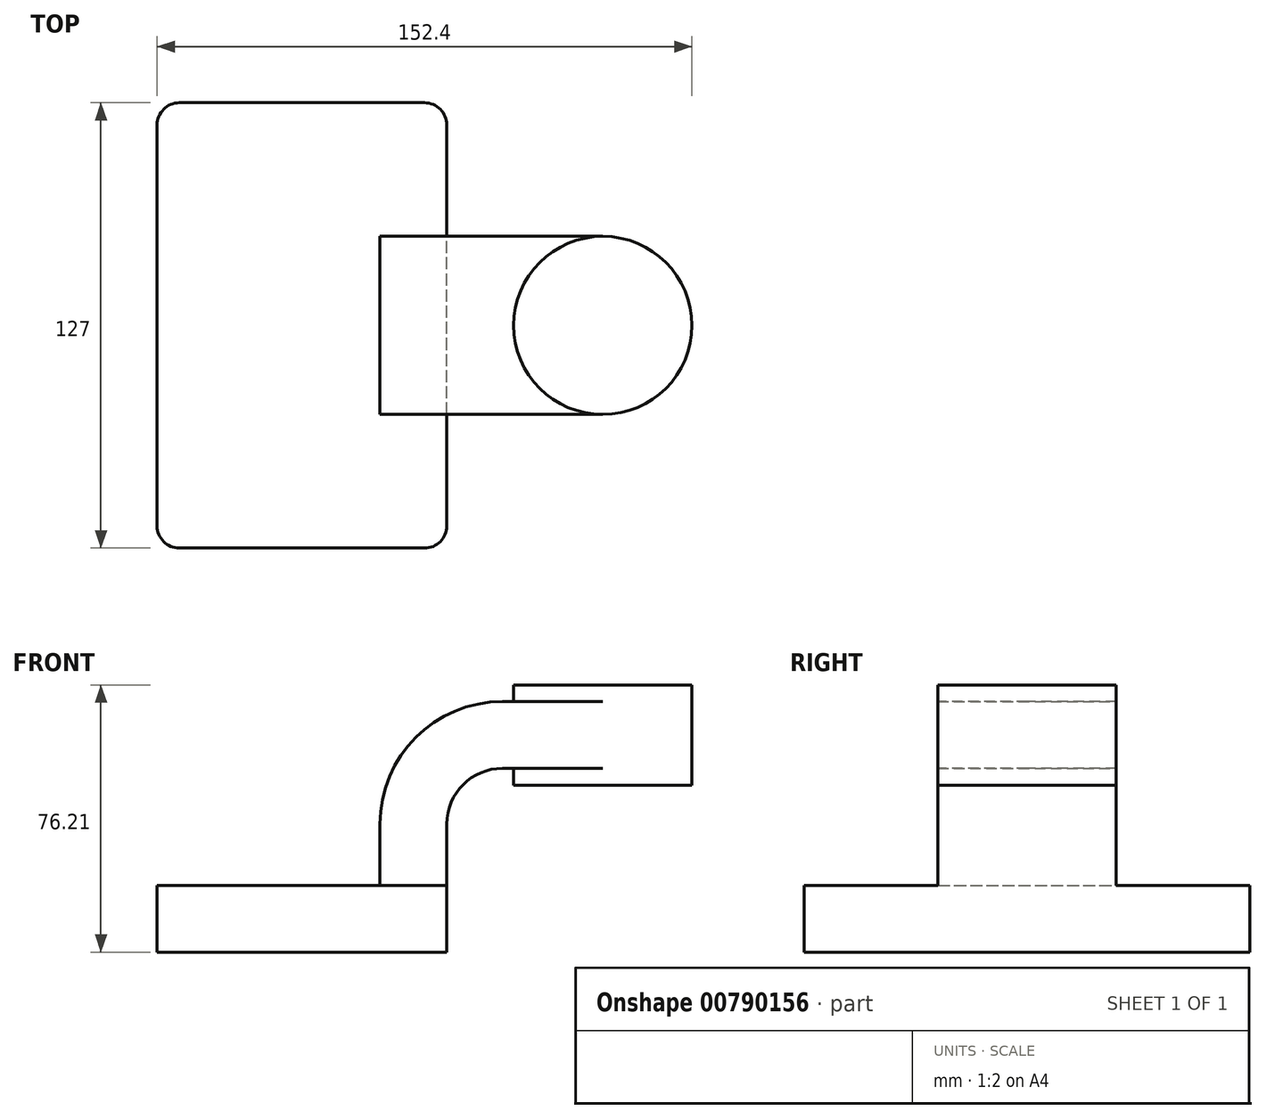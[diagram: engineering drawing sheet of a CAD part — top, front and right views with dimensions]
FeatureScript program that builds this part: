
annotation { "Feature Type Name" : "Feature", "Feature Type Description" : "" }
export const myFeature = defineFeature(function(context is Context, id is Id, definition is map)
    precondition{}
    {
        {
            var Q0;
            Q0=qCreatedBy(makeId("Front.planeOp"),FACE);
            var sketch = newSketch(context, id + "F0", { "sketchPlane" : qUnion([Q0])});
            skLineSegment(sketch, "E0.bottom", {"start": v(-41.27, -9.53) * mm, "end": v(41.28, -9.53) * mm});
            skLineSegment(sketch, "E0.top", {"start": v(-41.28, 9.52) * mm, "end": v(41.28, 9.52) * mm});
            skLineSegment(sketch, "E0.left", {"start": v(-41.28, -9.53) * mm, "end": v(-41.28, 9.52) * mm});
            skLineSegment(sketch, "E0.right", {"start": v(41.28, -9.53) * mm, "end": v(41.28, 9.52) * mm});
            skPoint(sketch, "E0.middle", {"position": v(0, 0) * mm});
            skLineSegment(sketch, "E1.bottom", {"start": v(60.32, 38.1) * mm, "end": v(111.12, 38.1) * mm});
            skLineSegment(sketch, "E1.top", {"start": v(60.32, 66.67) * mm, "end": v(111.12, 66.67) * mm});
            skLineSegment(sketch, "E1.left", {"start": v(60.32, 38.1) * mm, "end": v(60.32, 66.67) * mm});
            skLineSegment(sketch, "E1.right", {"start": v(111.12, 38.1) * mm, "end": v(111.12, 66.67) * mm});
            skPoint(sketch, "E1.middle", {"position": v(85.72, 52.39) * mm});
            skLineSegment(sketch, "E2", {"start": v(41.27, 9.52) * mm, "end": v(41.27, 27) * mm});
            skArc(sketch, "E3", {"start": v(41.27, 27) * mm, "mid": v(45.92, 38.23) * mm, "end": v(57.15, 42.88) * mm});
            skLineSegment(sketch, "E4", {"start": v(57.15, 42.88) * mm, "end": v(85.72, 42.88) * mm});
            skLineSegment(sketch, "E5.0", {"start": v(57.15, 61.93) * mm, "end": v(85.72, 61.93) * mm});
            skArc(sketch, "E5.1", {"start": v(22.23, 27) * mm, "mid": v(32.45, 51.7) * mm, "end": v(57.15, 61.93) * mm});
            skLineSegment(sketch, "E5.2", {"start": v(22.22, 9.52) * mm, "end": v(22.22, 27) * mm});
            skLineSegment(sketch, "E6", {"start": v(85.72, 38.1) * mm, "end": v(85.72, 66.67) * mm});
            skFitSpline(sketch, "E7", {"points": [v(-41.28, 9.52) * mm, v(57.15, 61.93) * mm], "startDerivative": vector(0, 74.97) * mm, "endDerivative": vector(109.8, 0) * mm});
            skSolve(sketch);
        }
        {
            var Q0;
            Q0=makeQuery(id+"F0.imprint","IMPRINT",FACE,{"disambiguationData":[TD([[makeQuery(id+"F0.imprint","IMPRINT",EDGE,{"derivedFrom":sQuery(id+"F0.wireOp",EDGE,"E0.bottom")}),1.0]])]});
            extrude(context, id + "F1", {"entities" : qUnion([Q0]), "endBound" : BoundingType.SYMMETRIC, "depth" : 127 * mm, "offsetDistance" : 25.4 * mm});
        }
        {
            var Q0;
            {var subQ1=sQuery(id+"F0.wireOp",EDGE,"E2");Q0=makeQuery(id+"F0.imprint","IMPRINT",FACE,{"disambiguationData":[TD([[makeQuery(id+"F0.imprint","IMPRINT",EDGE,{"derivedFrom":subQ1}),1.0]])]});}
            var Q1;
            {var subQ0=sQuery(id+"F0.wireOp",EDGE,"E4");var subQ1=sQuery(id+"F0.wireOp",EDGE,"E1.left");var subQ2=makeQuery(id+"F0.imprint","INTERSECT",VERTEX,{"derivedFrom":[subQ1,subQ0]});Q1=makeQuery(id+"F0.imprint","IMPRINT",FACE,{"disambiguationData":[TD([[makeQuery(id+"F0.imprint","IMPRINT",EDGE,{"disambiguationData":[TD([[subQ2,-1.0]])],"derivedFrom":subQ1}),-1.0]])]});}
            extrude(context, id + "F2", {"entities" : qUnion([Q0, Q1]), "operationType" : NewBodyOperationType.ADD, "endBound" : BoundingType.SYMMETRIC, "depth" : 50.8 * mm, "offsetDistance" : 25.4 * mm});
        }
        {
            var Q0;
            Q0=makeQuery(id+"F0.imprint","IMPRINT",FACE,{"disambiguationData":[TD([[makeQuery(id+"F0.imprint","IMPRINT",EDGE,{"derivedFrom":sQuery(id+"F0.wireOp",EDGE,"E5.1")}),1.0]])]});
            extrude(context, id + "F3", {"entities" : qUnion([Q0]), "operationType" : NewBodyOperationType.ADD, "endBound" : BoundingType.SYMMETRIC, "depth" : 15.88 * mm, "offsetDistance" : 25.4 * mm});
        }
        {
            var Q0;
            {var subQ0=sQuery(id+"F0.wireOp",EDGE,"E1.right");Q0=makeQuery(id+"F0.imprint","IMPRINT",FACE,{"disambiguationData":[TD([[makeQuery(id+"F0.imprint","IMPRINT",EDGE,{"derivedFrom":subQ0}),1.0]])]});}
            var Q1;
            Q1=sQuery(id+"F0.wireOp",EDGE,"E6");
            revolve(context, id + "F4", {"operationType" : NewBodyOperationType.ADD, "surfaceOperationType" : NewSurfaceOperationType.NEW, "entities" : qUnion([Q0]), "axis" : qUnion([Q1]), "revolveType" : RevolveType.FULL});
        }
        {
            var Q0;
            Q0=makeQuery(id+"F1.opExtrude","CAP_EDGE",EDGE,{"disambiguationData":[OSD([sQuery(id+"F0.wireOp",EDGE,"E0.right")])],"isStart":false});
            var Q1;
            Q1=makeQuery(id+"F1.opExtrude","CAP_EDGE",EDGE,{"disambiguationData":[OSD([sQuery(id+"F0.wireOp",EDGE,"E0.left")])],"isStart":false});
            var Q2;
            Q2=makeQuery(id+"F1.opExtrude","CAP_EDGE",EDGE,{"disambiguationData":[OSD([sQuery(id+"F0.wireOp",EDGE,"E0.right")])],"isStart":true});
            var Q3;
            Q3=makeQuery(id+"F1.opExtrude","CAP_EDGE",EDGE,{"disambiguationData":[OSD([sQuery(id+"F0.wireOp",EDGE,"E0.left")])],"isStart":true});
            fillet(context, id + "F5", {"entities" : qUnion([Q0, Q1, Q2, Q3]), "radius" : 6.35 * mm, "tangentPropagation" : true, "allowEdgeOverflow" : false});
        }
    });
